FCSTD DOCUMENT  (FreeCAD 0.16R4905 +21 (Git))
Label: hex_tiling_skewed
License: All rights reserved
LicenseURL: http://en.wikipedia.org/wiki/All_rights_reserved
objects: Part::FeaturePython×5, Part::Part2DObjectPython×4, Sketcher::SketchObject×3
note: 12 computed .brp shape members not serialized (recipe doc carries the construction recipe); baked Part::Feature solids carry a one-line shape summary decoded from their .brp

FEATURE [Sketcher::SketchObject] Sketch  label="Sk-Tile"
  sketch-geometry (7):
    g0: LineSegment StartX=11.1203 StartY=-10.4495 StartZ=0 EndX=14.6097 EndY=4.40569 EndZ=0
    g1: LineSegment StartX=14.6097 StartY=4.40569 StartZ=0 EndX=3.48942 EndY=14.8552 EndZ=0
    g2: LineSegment StartX=3.48942 StartY=14.8552 StartZ=0 EndX=-11.1203 EndY=10.4495 EndZ=0
    g3: LineSegment StartX=-11.1203 StartY=10.4495 StartZ=0 EndX=-14.6097 EndY=-4.40569 EndZ=0
    g4: LineSegment StartX=-14.6097 StartY=-4.40569 StartZ=0 EndX=-3.48942 EndY=-14.8552 EndZ=0
    g5: LineSegment StartX=-3.48942 StartY=-14.8552 StartZ=0 EndX=11.1203 EndY=-10.4495 EndZ=0
    g6: Circle [constr] CenterX=0 CenterY=0 CenterZ=0 NormalX=0 NormalY=0 NormalZ=1 Radius=15.2596
  constraints (14):
    c: Coincident(g0,g1)
    c: Coincident(g1,g2)
    c: Coincident(g2,g3)
    c: Coincident(g3,g4)
    c: Coincident(g4,g5)
    c: Coincident(g5,g0)
    c: Equal(g0, g1-g5) x5
    c: PointOnObject(g0,g6)
    c: PointOnObject(g1,g6)
    c: PointOnObject(g2,g6)
    c: PointOnObject(g3,g6)
    c: PointOnObject(g4,g6)
    c: PointOnObject(g5,g6)
    c: Coincident(g6,g-1)
FEATURE [Sketcher::SketchObject] Sketch001
  ExternalGeometry = -> [Sketch]
  sketch-geometry (3):
    g0: LineSegment StartX=0 StartY=0 StartZ=0 EndX=25.73 EndY=-6.04386 EndZ=0
    g1: LineSegment StartX=25.73 StartY=-6.04386 StartZ=0 EndX=18.0991 EndY=19.2609 EndZ=0
    g2: LineSegment StartX=18.0991 StartY=19.2609 StartZ=0 EndX=43.8292 EndY=13.2171 EndZ=0
  constraints (7):
    c: Coincident(g0,g1)
    c: Coincident(g1,g2)
    c: Symmetric(g0,g1,g-4)
    c: Coincident(g0,g-1)
    c: Symmetric(g0,g-1,g-3)
    c: Parallel(g2,g0)
    c: Equal(g2,g0)
FEATURE [Part::Part2DObjectPython] Clone2D  label="Clone of Sketch001 (2D)"  # Draft 2D object (typed FeaturePython)
  MapMode = 1
  Objects = -> [Sketch001]
  Scale = (2,2,2)
FEATURE [Part::Part2DObjectPython] Clone2D001  label="Clone of Clone of Sketch001 (2D) (2D)"  # Draft 2D object (typed FeaturePython)
  MapMode = 1
  Objects = -> [Clone2D]
  Scale = (2,2,2)
FEATURE [Part::Part2DObjectPython] Clone2D002  label="Clone of Clone of Clone of Sketch001 (2D) (2D) (2D)"  # Draft 2D object (typed FeaturePython)
  MapMode = 1
  Objects = -> [Clone2D001]
  Scale = (2,2,2)
FEATURE [Part::Part2DObjectPython] Clone2D003  label="Clone of Clone of Clone of Clone of Sketch001 (2D) (2D) (2D) (2D)"  # Draft 2D object (typed FeaturePython)
  MapMode = 1
  Objects = -> [Clone2D002]
  Scale = (2,2,2)
FEATURE [Sketcher::SketchObject] Sketch002  label="Sk-Hole"
  ExternalGeometry = -> [Sketch]
  sketch-geometry (7):
    g0: LineSegment StartX=12.3987 StartY=3.73892 StartZ=0 EndX=2.96133 EndY=12.607 EndZ=0
    g1: LineSegment StartX=2.96133 StartY=12.607 StartZ=0 EndX=-9.43734 EndY=8.8681 EndZ=0
    g2: LineSegment StartX=-9.43734 StartY=8.8681 StartZ=0 EndX=-12.3987 EndY=-3.73892 EndZ=0
    g3: LineSegment StartX=-12.3987 StartY=-3.73892 StartZ=0 EndX=-2.96133 EndY=-12.607 EndZ=0
    g4: LineSegment StartX=-2.96133 StartY=-12.607 StartZ=0 EndX=9.43734 EndY=-8.8681 EndZ=0
    g5: LineSegment StartX=9.43734 StartY=-8.8681 StartZ=0 EndX=12.3987 EndY=3.73892 EndZ=0
    g6: Circle [constr] CenterX=0 CenterY=0 CenterZ=0 NormalX=0 NormalY=0 NormalZ=1 Radius=12.9502
  constraints (16):
    c: Coincident(g0,g1)
    c: Coincident(g1,g2)
    c: Coincident(g2,g3)
    c: Coincident(g3,g4)
    c: Coincident(g4,g5)
    c: Coincident(g5,g0)
    c: Equal(g0, g1-g5) x5
    c: PointOnObject(g0,g6)
    c: PointOnObject(g1,g6)
    c: PointOnObject(g2,g6)
    c: PointOnObject(g3,g6)
    c: PointOnObject(g4,g6)
    c: PointOnObject(g5,g6)
    c: Parallel(g0,g-3)
    c: Coincident(g6,g-1)
    c: Distance(g0,g-3) = 2
FEATURE [Part::FeaturePython] PathArray  # WARN: FeaturePython — macro-defined, semantics opaque (R4)
  Align = false
  Base = -> Sketch002
  Count = 4
  PathObj = -> Sketch001
  Xlate = (0,0,0)
FEATURE [Part::FeaturePython] PathArray001  # WARN: FeaturePython — macro-defined, semantics opaque (R4)
  Align = false
  Base = -> PathArray
  Count = 4
  PathObj = -> Clone2D
  Xlate = (0,0,0)
FEATURE [Part::FeaturePython] PathArray002  # WARN: FeaturePython — macro-defined, semantics opaque (R4)
  Align = false
  Base = -> PathArray001
  Count = 4
  PathObj = -> Clone2D001
  Xlate = (0,0,0)
FEATURE [Part::FeaturePython] PathArray003  # WARN: FeaturePython — macro-defined, semantics opaque (R4)
  Align = false
  Base = -> PathArray002
  Count = 4
  PathObj = -> Clone2D002
  Xlate = (0,0,0)
FEATURE [Part::FeaturePython] PathArray004  # WARN: FeaturePython — macro-defined, semantics opaque (R4)
  Align = false
  Base = -> PathArray003
  Count = 4
  PathObj = -> Clone2D003
  Xlate = (0,0,0)
